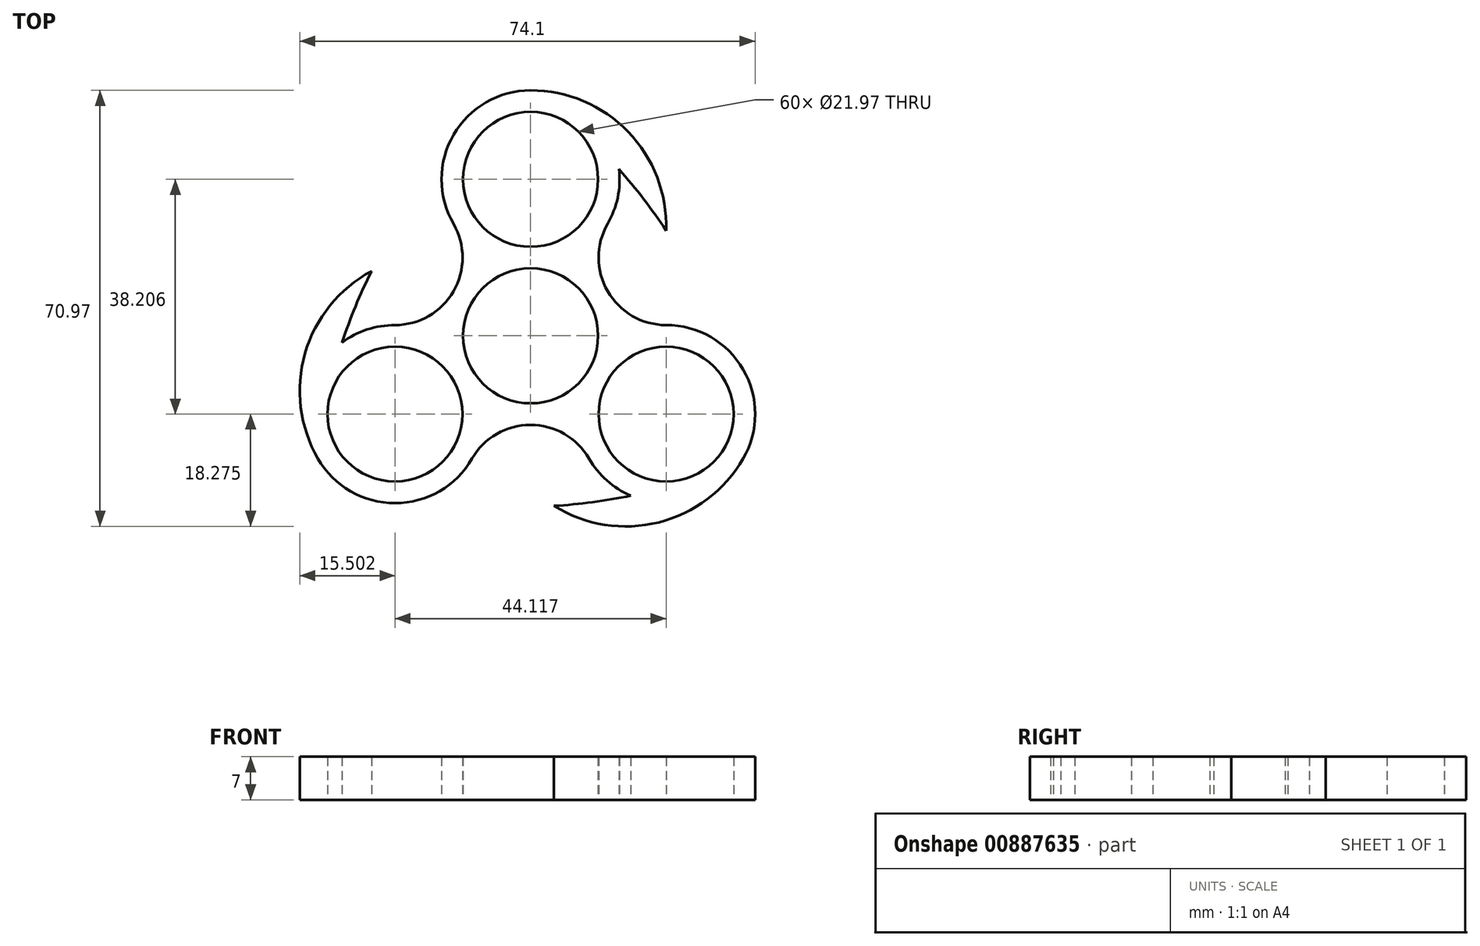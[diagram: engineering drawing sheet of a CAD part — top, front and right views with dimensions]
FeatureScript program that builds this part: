
annotation { "Feature Type Name" : "Feature", "Feature Type Description" : "" }
export const myFeature = defineFeature(function(context is Context, id is Id, definition is map)
    precondition{}
    {
        {
            var Q0;
            Q0=qCreatedBy(makeId("Top.planeOp"),FACE);
            var sketch = newSketch(context, id + "F0", { "sketchPlane" : qUnion([Q0])});
            skCircle(sketch, "E0", {"center": v(0, 0) * mm, "radius": 10.99 * mm});
            skCircle(sketch, "E1", {"center": v(0, 0) * mm, "radius": 25.47 * mm, "construction": true});
            skCircle(sketch, "E2", {"center": v(0, 25.47) * mm, "radius": 10.99 * mm});
            skCircle(sketch, "E3", {"center": v(-22.06, -12.74) * mm, "radius": 10.99 * mm});
            skCircle(sketch, "E4", {"center": v(22.06, -12.74) * mm, "radius": 10.99 * mm});
            skLineSegment(sketch, "E5", {"start": v(-22.06, -12.74) * mm, "end": v(22.06, -12.74) * mm, "construction": true});
            skLineSegment(sketch, "E6", {"start": v(0, 25.47) * mm, "end": v(-22.06, -12.74) * mm, "construction": true});
            skLineSegment(sketch, "E7", {"start": v(22.06, -12.74) * mm, "end": v(0, 25.47) * mm, "construction": true});
            skLineSegment(sketch, "E8.bottom", {"start": v(-57.15, 57.15) * mm, "end": v(57.15, 57.15) * mm, "construction": true});
            skLineSegment(sketch, "E8.top", {"start": v(-57.15, -57.15) * mm, "end": v(57.15, -57.15) * mm, "construction": true});
            skLineSegment(sketch, "E8.left", {"start": v(-57.15, 57.15) * mm, "end": v(-57.15, -57.15) * mm, "construction": true});
            skLineSegment(sketch, "E8.right", {"start": v(57.15, 57.15) * mm, "end": v(57.15, -57.15) * mm, "construction": true});
            skPoint(sketch, "E9", {"position": v(-57.15, 0) * mm});
            skPoint(sketch, "E10", {"position": v(0, 57.15) * mm});
            skSolve(sketch);
        }
        {
            var Q0;
            Q0=qCreatedBy(makeId("Top.planeOp"),FACE);
            var sketch = newSketch(context, id + "F1", { "sketchPlane" : qUnion([Q0])});
            skCircle(sketch, "E11", {"center": v(0, 0) * mm, "radius": 10.99 * mm});
            skCircle(sketch, "E12", {"center": v(-22.06, -12.74) * mm, "radius": 10.99 * mm});
            skCircle(sketch, "E13", {"center": v(0, 25.47) * mm, "radius": 10.99 * mm});
            skCircle(sketch, "E14", {"center": v(22.06, -12.74) * mm, "radius": 10.99 * mm});
            skLineSegment(sketch, "E15.bottom", {"start": v(-57.15, 57.15) * mm, "end": v(57.15, 57.15) * mm, "construction": true});
            skLineSegment(sketch, "E15.top", {"start": v(-57.15, -57.15) * mm, "end": v(57.15, -57.15) * mm, "construction": true});
            skLineSegment(sketch, "E15.left", {"start": v(-57.15, 57.15) * mm, "end": v(-57.15, -57.15) * mm, "construction": true});
            skLineSegment(sketch, "E15.right", {"start": v(57.15, 57.15) * mm, "end": v(57.15, -57.15) * mm, "construction": true});
            skPoint(sketch, "E16", {"position": v(-57.15, 0) * mm});
            skPoint(sketch, "E17", {"position": v(0, 57.15) * mm});
            skArc(sketch, "E18", {"start": v(-22.06, 1.75) * mm, "mid": v(-26.6, 1.02) * mm, "end": v(-30.68, -1.1) * mm});
            skArc(sketch, "E19", {"start": v(12.54, 18.23) * mm, "mid": v(14.18, 22.52) * mm, "end": v(14.4, 27.11) * mm});
            skArc(sketch, "E20", {"start": v(9.51, -19.98) * mm, "mid": v(12.41, -23.54) * mm, "end": v(16.29, -26.02) * mm});
            skArc(sketch, "E21", {"start": v(-22.06, 1.75) * mm, "mid": v(-12.54, 7.24) * mm, "end": v(-12.54, 18.23) * mm});
            skArc(sketch, "E22", {"start": v(12.54, 18.23) * mm, "mid": v(12.54, 7.24) * mm, "end": v(22.06, 1.75) * mm});
            skArc(sketch, "E23", {"start": v(9.51, -19.98) * mm, "mid": v(0, -14.49) * mm, "end": v(-9.51, -19.98) * mm});
            skCircle(sketch, "E24", {"center": v(0, 0) * mm, "radius": 14.49 * mm, "construction": true});
            skArc(sketch, "E25", {"start": v(22.06, 17.14) * mm, "mid": v(15.87, 33.23) * mm, "end": v(0, 39.96) * mm});
            skArc(sketch, "E26", {"start": v(22.06, 17.14) * mm, "mid": v(18.4, 22.27) * mm, "end": v(14.4, 27.11) * mm});
            skArc(sketch, "E27.1.0", {"start": v(-25.87, 10.53) * mm, "mid": v(-28.5, 4.8) * mm, "end": v(-30.68, -1.1) * mm});
            skArc(sketch, "E27.1.1", {"start": v(-25.87, 10.53) * mm, "mid": v(-36.7, -2.87) * mm, "end": v(-34.6, -19.98) * mm});
            skArc(sketch, "E27.2.0", {"start": v(3.82, -27.67) * mm, "mid": v(10.08, -27.08) * mm, "end": v(16.29, -26.02) * mm});
            skArc(sketch, "E27.2.1", {"start": v(3.82, -27.67) * mm, "mid": v(20.84, -30.35) * mm, "end": v(34.6, -19.98) * mm});
            skArc(sketch, "E28.trimOffspring", {"start": v(0, 39.96) * mm, "mid": v(-12.54, 32.71) * mm, "end": v(-12.54, 18.23) * mm});
            skArc(sketch, "E29.trimOffspring", {"start": v(34.6, -19.98) * mm, "mid": v(34.6, -5.5) * mm, "end": v(22.06, 1.75) * mm});
            skArc(sketch, "E30.trimOffspring", {"start": v(-34.6, -19.98) * mm, "mid": v(-22.06, -27.22) * mm, "end": v(-9.51, -19.98) * mm});
            skSolve(sketch);
        }
        {
            var Q0;
            Q0=makeQuery(id+"F1.imprint","IMPRINT",FACE,{"disambiguationData":[TD([[makeQuery(id+"F1.imprint","IMPRINT",EDGE,{"derivedFrom":sQuery(id+"F1.wireOp",EDGE,"E11")}),-1.0]])]});
            extrude(context, id + "F2", {"entities" : qUnion([Q0]), "depth" : 7 * mm, "offsetDistance" : 25.4 * mm});
        }
    });
